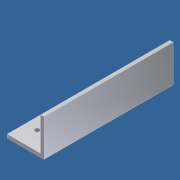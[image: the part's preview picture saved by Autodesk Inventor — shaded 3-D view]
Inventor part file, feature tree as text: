
AUTODESK INVENTOR PART (.ipt)
format: ipt  version: 2012 (Build 160160000, 160)  size: 79,872 bytes
history: native  units: in
note: dims shown in document units (in); Inventor stores cm internally (conversion verified against a paired STEP export)
features: hole x2, extrude x1, sketch x1
ambient origin geometry x8: Origin, YZ Plane, XZ Plane, XY Plane, X Axis, Y Axis, Z Axis, Center Point
bodies: Solid1 (feature_tree)
feature tree (4):
  extrude  "Extrusion1"  Depth=0.188in
  hole  "Hole1"  [1 undecoded]
  hole  "Hole2"  [1 undecoded]
  sketch  "Sketch1"  dims[d0=2.0in d1=0.188in d2=7.0in d3=0.0in d4=1.0in d5=0.625in d6=0.265in d7=0.75in d8=0.375in d9=0.25in d10=0.5635in d11=1.0in d12=0.8108in d13=1.0in d14=0.625in d15=0.265in d16=0.75in d17=0.375in d18=0.25in d19=0.5635in d20=1.0in d21=0.8108in]
note: 2 required parameter values undecoded (feature->parameter linkage not recoverable at this tier; creation-order binding heuristic only, values carry confidence <= 0.55)
